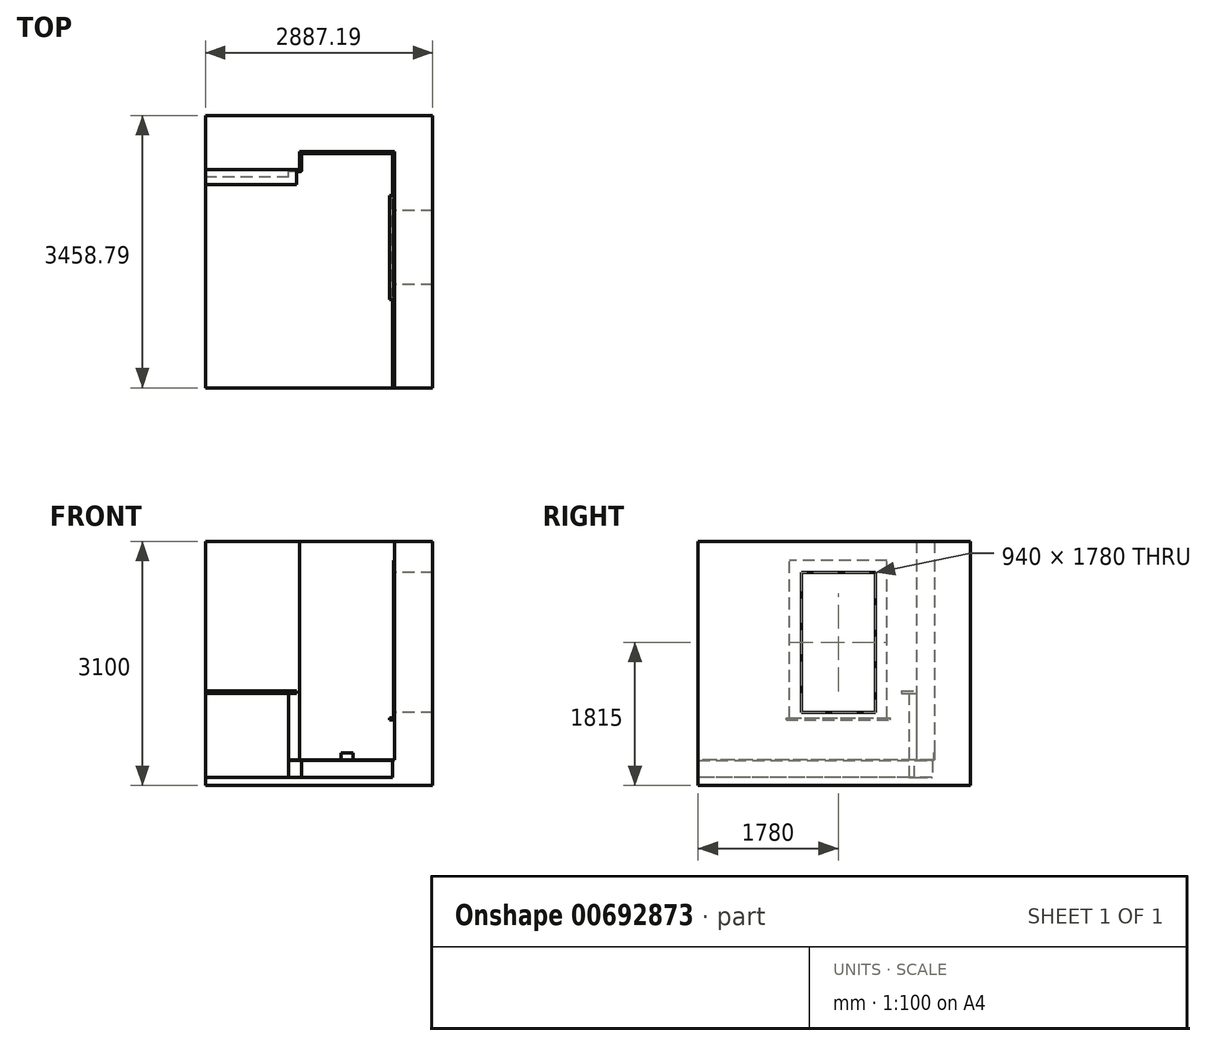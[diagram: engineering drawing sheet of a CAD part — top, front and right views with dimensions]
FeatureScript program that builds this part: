
annotation { "Feature Type Name" : "Feature", "Feature Type Description" : "" }
export const myFeature = defineFeature(function(context is Context, id is Id, definition is map)
    precondition{}
    {
        {
            var Q0;
            Q0=qCreatedBy(makeId("Top.planeOp"),FACE);
            var sketch = newSketch(context, id + "F0", { "sketchPlane" : qUnion([Q0])});
            skLineSegment(sketch, "E0", {"start": v(0, 0) * mm, "end": v(0, 225) * mm});
            skLineSegment(sketch, "E1", {"start": v(0, 225) * mm, "end": v(1200, 225) * mm});
            skLineSegment(sketch, "E2", {"start": v(1200, 225) * mm, "end": v(1200, -2775) * mm});
            skLineSegment(sketch, "E3", {"start": v(0, 0) * mm, "end": v(-1200, 0) * mm});
            skLineSegment(sketch, "E4", {"start": v(-1200, 0) * mm, "end": v(-1200, 683.8) * mm});
            skLineSegment(sketch, "E5", {"start": v(-1200, 683.8) * mm, "end": v(1687.2, 683.8) * mm});
            skLineSegment(sketch, "E6", {"start": v(1687.2, 683.8) * mm, "end": v(1687.2, -2775) * mm});
            skLineSegment(sketch, "E7", {"start": v(1687.2, -2775) * mm, "end": v(1200, -2775) * mm});
            skSolve(sketch);
        }
        {
            var Q0;
            Q0 = qSketchRegion(id + "F0", true);
            extrude(context, id + "F1", {"entities" : qUnion([Q0]), "depth" : 3000 * mm, "offsetDistance" : 25 * mm});
        }
        {
            var Q0;
            Q0=qCreatedBy(makeId("Top.planeOp"),FACE);
            var sketch = newSketch(context, id + "F2", { "sketchPlane" : qUnion([Q0])});
            skLineSegment(sketch, "E8.bottom", {"start": v(1687.2, 683.8) * mm, "end": v(-1200, 683.8) * mm});
            skLineSegment(sketch, "E8.top", {"start": v(1687.2, -2775) * mm, "end": v(-1200, -2775) * mm});
            skLineSegment(sketch, "E8.left", {"start": v(1687.2, 683.8) * mm, "end": v(1687.2, -2775) * mm});
            skLineSegment(sketch, "E8.right", {"start": v(-1200, 683.8) * mm, "end": v(-1200, -2775) * mm});
            skSolve(sketch);
        }
        {
            var Q0;
            Q0 = qSketchRegion(id + "F2", true);
            extrude(context, id + "F3", {"entities" : qUnion([Q0]), "operationType" : NewBodyOperationType.ADD, "oppositeDirection" : true, "depth" : 100 * mm, "offsetDistance" : 25 * mm});
        }
        {
            var Q0;
            Q0=makeQuery(id+"F1.opExtrude","SWEPT_FACE",FACE,{"disambiguationData":[OSD([sQuery(id+"F0.wireOp",EDGE,"E2")])]});
            var sketch = newSketch(context, id + "F4", { "sketchPlane" : qUnion([Q0])});
            skLineSegment(sketch, "E9.bottom", {"start": v(1655, 730) * mm, "end": v(335, 730) * mm});
            skLineSegment(sketch, "E9.top", {"start": v(1655, 755) * mm, "end": v(335, 755) * mm});
            skLineSegment(sketch, "E9.left", {"start": v(1655, 730) * mm, "end": v(1655, 755) * mm});
            skLineSegment(sketch, "E9.right", {"start": v(335, 730) * mm, "end": v(335, 755) * mm});
            skSolve(sketch);
        }
        {
            var Q0;
            Q0 = qSketchRegion(id + "F4", true);
            extrude(context, id + "F5", {"entities" : qUnion([Q0]), "operationType" : NewBodyOperationType.ADD, "depth" : 60 * mm, "offsetDistance" : 25 * mm});
        }
        {
            var Q0;
            Q0=makeQuery(id+"F1.opExtrude","SWEPT_FACE",FACE,{"disambiguationData":[OSD([sQuery(id+"F0.wireOp",EDGE,"E2")])]});
            var sketch = newSketch(context, id + "F6", { "sketchPlane" : qUnion([Q0])});
            skLineSegment(sketch, "E10.bottom", {"start": v(375, 755) * mm, "end": v(1615, 755) * mm});
            skLineSegment(sketch, "E10.top", {"start": v(375, 2755) * mm, "end": v(1615, 2755) * mm});
            skLineSegment(sketch, "E10.left", {"start": v(375, 755) * mm, "end": v(375, 2755) * mm});
            skLineSegment(sketch, "E10.right", {"start": v(1615, 755) * mm, "end": v(1615, 2755) * mm});
            skSolve(sketch);
        }
        {
            var Q0;
            Q0 = qSketchRegion(id + "F6", true);
            extrude(context, id + "F7", {"entities" : qUnion([Q0]), "operationType" : NewBodyOperationType.ADD, "depth" : 10 * mm, "offsetDistance" : 25 * mm});
        }
        {
            var Q0;
            Q0=makeQuery(id+"F7.opExtrude","CAP_FACE",FACE,{"disambiguationData":[OSD([sQuery(id+"F6.wireOp",EDGE,"E10.bottom"),sQuery(id+"F6.wireOp",EDGE,"E10.top"),sQuery(id+"F6.wireOp",EDGE,"E10.left"),sQuery(id+"F6.wireOp",EDGE,"E10.right")])],"isStart":false});
            var sketch = newSketch(context, id + "F8", { "sketchPlane" : qUnion([Q0])});
            skLineSegment(sketch, "E11.bottom", {"start": v(1465, 2605) * mm, "end": v(525, 2605) * mm});
            skLineSegment(sketch, "E11.top", {"start": v(1465, 825) * mm, "end": v(525, 825) * mm});
            skLineSegment(sketch, "E11.left", {"start": v(1465, 2605) * mm, "end": v(1465, 825) * mm});
            skLineSegment(sketch, "E11.right", {"start": v(525, 2605) * mm, "end": v(525, 825) * mm});
            skSolve(sketch);
        }
        {
            var Q0;
            Q0 = qSketchRegion(id + "F8", true);
            extrude(context, id + "F9", {"entities" : qUnion([Q0]), "operationType" : NewBodyOperationType.REMOVE, "endBound" : BoundingType.UP_TO_NEXT, "oppositeDirection" : true, "depth" : 25 * mm, "offsetDistance" : 25 * mm});
        }
        {
            var Q0;
            Q0=makeQuery(id+"F3.opExtrude","CAP_FACE",FACE,{"disambiguationData":[OSD([sQuery(id+"F2.wireOp",EDGE,"E8.bottom"),sQuery(id+"F2.wireOp",EDGE,"E8.top"),sQuery(id+"F2.wireOp",EDGE,"E8.left"),sQuery(id+"F2.wireOp",EDGE,"E8.right")])],"isStart":true});
            var sketch = newSketch(context, id + "F10", { "sketchPlane" : qUnion([Q0])});
            skLineSegment(sketch, "E12.0", {"start": v(25, -25) * mm, "end": v(-1200, -25) * mm});
            skLineSegment(sketch, "E12.1", {"start": v(25, -25) * mm, "end": v(25, 200) * mm});
            skLineSegment(sketch, "E12.2", {"start": v(25, 200) * mm, "end": v(1175, 200) * mm});
            skLineSegment(sketch, "E12.3", {"start": v(1175, 200) * mm, "end": v(1175, -2775) * mm});
            skLineSegment(sketch, "E13.0", {"start": v(0, 0) * mm, "end": v(-1200, 0) * mm});
            skLineSegment(sketch, "E13.1", {"start": v(0, 0) * mm, "end": v(0, 225) * mm});
            skLineSegment(sketch, "E13.2", {"start": v(0, 225) * mm, "end": v(1200, 225) * mm});
            skLineSegment(sketch, "E13.3", {"start": v(1200, 225) * mm, "end": v(1200, -2775) * mm});
            skLineSegment(sketch, "E14", {"start": v(-1200, 0) * mm, "end": v(-1200, -25) * mm});
            skLineSegment(sketch, "E15", {"start": v(1175, -2775) * mm, "end": v(1200, -2775) * mm});
            skSolve(sketch);
        }
        {
            var Q0;
            Q0 = qSketchRegion(id + "F10", true);
            extrude(context, id + "F11", {"entities" : qUnion([Q0]), "operationType" : NewBodyOperationType.ADD, "depth" : 225 * mm, "offsetDistance" : 25 * mm});
        }
        {
            var Q0;
            Q0=makeQuery(id+"F11.opExtrude","SWEPT_EDGE",EDGE,{"disambiguationData":[OSD([sQuery(id+"F10.wireOp",EDGE,"E12.0"),sQuery(id+"F10.wireOp",EDGE,"E12.1")])]});
            var Q1;
            Q1=makeQuery(id+"F11.opExtrude","SWEPT_EDGE",EDGE,{"disambiguationData":[OSD([sQuery(id+"F10.wireOp",EDGE,"E12.1"),sQuery(id+"F10.wireOp",EDGE,"E12.2")])]});
            var Q2;
            Q2=makeQuery(id+"F11.opExtrude","SWEPT_EDGE",EDGE,{"disambiguationData":[OSD([sQuery(id+"F10.wireOp",EDGE,"E12.2"),sQuery(id+"F10.wireOp",EDGE,"E12.3")])]});
            fillet(context, id + "F12", {"entities" : qUnion([Q0, Q1, Q2]), "radius" : 10 * mm, "tangentPropagation" : true, "allowEdgeOverflow" : false});
        }
        {
            var Q0;
            Q0=makeQuery(id+"F11.opExtrude","CAP_EDGE",EDGE,{"disambiguationData":[OSD([sQuery(id+"F10.wireOp",EDGE,"E12.0")])],"isStart":false});
            chamfer(context, id + "F13", {"entities" : qUnion([Q0]), "width" : 10 * mm, "tangentPropagation" : true});
        }
        {
            var Q0;
            Q0=makeQuery(id+"F1.opExtrude","SWEPT_FACE",FACE,{"disambiguationData":[OSD([sQuery(id+"F0.wireOp",EDGE,"E3")])]});
            var sketch = newSketch(context, id + "F14", { "sketchPlane" : qUnion([Q0])});
            skLineSegment(sketch, "E16.bottom", {"start": v(-40, 1100) * mm, "end": v(-1200, 1100) * mm});
            skLineSegment(sketch, "E16.top", {"start": v(-40, 1070) * mm, "end": v(-1200, 1070) * mm});
            skLineSegment(sketch, "E16.left", {"start": v(-40, 1100) * mm, "end": v(-40, 1070) * mm});
            skLineSegment(sketch, "E16.right", {"start": v(-1200, 1100) * mm, "end": v(-1200, 1070) * mm});
            skSolve(sketch);
        }
        {
            var Q0;
            Q0 = qSketchRegion(id + "F14", true);
            extrude(context, id + "F15", {"entities" : qUnion([Q0]), "operationType" : NewBodyOperationType.ADD, "depth" : 190 * mm, "offsetDistance" : 25 * mm});
        }
        {
            var Q0;
            Q0=makeQuery(id+"F1.opExtrude","SWEPT_FACE",FACE,{"disambiguationData":[OSD([sQuery(id+"F0.wireOp",EDGE,"E3")])]});
            var sketch = newSketch(context, id + "F16", { "sketchPlane" : qUnion([Q0])});
            skLineSegment(sketch, "E17.bottom", {"start": v(-140, 1070) * mm, "end": v(-1200, 1070) * mm});
            skLineSegment(sketch, "E17.top", {"start": v(-140, 0) * mm, "end": v(-1200, 0) * mm});
            skLineSegment(sketch, "E17.left", {"start": v(-140, 1070) * mm, "end": v(-140, 0) * mm});
            skLineSegment(sketch, "E17.right", {"start": v(-1200, 1070) * mm, "end": v(-1200, 0) * mm});
            skSolve(sketch);
        }
        {
            var Q0;
            Q0 = qSketchRegion(id + "F16", true);
            extrude(context, id + "F17", {"entities" : qUnion([Q0]), "operationType" : NewBodyOperationType.ADD, "depth" : 100 * mm, "offsetDistance" : 25 * mm});
        }
        {
            var Q0;
            Q0=makeQuery(id+"F1.opExtrude","SWEPT_FACE",FACE,{"disambiguationData":[OSD([sQuery(id+"F0.wireOp",EDGE,"E1")])]});
            var sketch = newSketch(context, id + "F18", { "sketchPlane" : qUnion([Q0])});
            skLineSegment(sketch, "E18.bottom", {"start": v(525, 315) * mm, "end": v(675, 315) * mm});
            skLineSegment(sketch, "E18.top", {"start": v(525, 225) * mm, "end": v(675, 225) * mm});
            skLineSegment(sketch, "E18.left", {"start": v(525, 315) * mm, "end": v(525, 225) * mm});
            skLineSegment(sketch, "E18.right", {"start": v(675, 315) * mm, "end": v(675, 225) * mm});
            skLineSegment(sketch, "E19", {"start": v(0, 315) * mm, "end": v(1200, 315) * mm, "construction": true});
            skPoint(sketch, "E20", {"position": v(600, 315) * mm});
            skSolve(sketch);
        }
        {
            var Q0;
            Q0 = qSketchRegion(id + "F18", true);
            extrude(context, id + "F19", {"entities" : qUnion([Q0]), "operationType" : NewBodyOperationType.ADD, "depth" : 10 * mm, "offsetDistance" : 25 * mm});
        }
    });
